# Revit family: fire_rinnai_arriva752
name_source: partatom
category: Specialty Equipment
revit_build: Autodesk Revit 2015 (Build: 20140905_0730(x64)
units: mm (PartAtom-declared; Revit-internal decimal feet)

## types (3) — shared parameters
Manufacturer = Rinnai NZ Ltd
Model = Arriva 752
URL = www.rinnai.co.nz
_fire_centrewidth = 750 mm  [stored 2.46063 ft]
_fire_clearceiling = 1000 mm  [stored 3.28084 ft]
_fire_cleardepth = 1000 mm  [stored 3.28084 ft]
_fire_clearheight = 400 mm  [stored 1.31234 ft]
_fire_clearwidth = 1500 mm  [stored 4.92126 ft]
_fire_side_clearance = 400 mm  [stored 1.31234 ft]
_fire_top = 705 mm  [stored 2.31299 ft]
_fire_width = 1050 mm  [stored 3.44488 ft]
_fire_window_top = 485 mm  [stored 1.59121 ft]
_fire_window_width = 700 mm  [stored 2.29659 ft]
_opening_height = 655 mm  [stored 2.14895 ft]
_opening_width = 840 mm  [stored 2.75591 ft]
clearance = 5 mm  [stored 0.0164042 ft]
m_plinth = <By Category>
opening floor offset = 2 mm  [stored 0.00656168 ft]
v_fireplace = Yes

## per-type parameters (varying)
| type | Description | _opening_depth |
| arriva752_underfloor | Arriva 750 Underfloor | 500 mm  [stored 1.64042 ft] |
| arriva752_extend | Arriva 752 Extended | 475 mm  [stored 1.5584 ft] |
| arriva752_direct | Arriva 752 Direct | 380 mm  [stored 1.24672 ft] |

note: [stored X ft] marks values corroborated as IEEE doubles in the binary element streams (Revit-internal decimal feet)

## geometry (parser evidence)
native form markers: Sweep x19
no freeform markers — native parametric forms only
